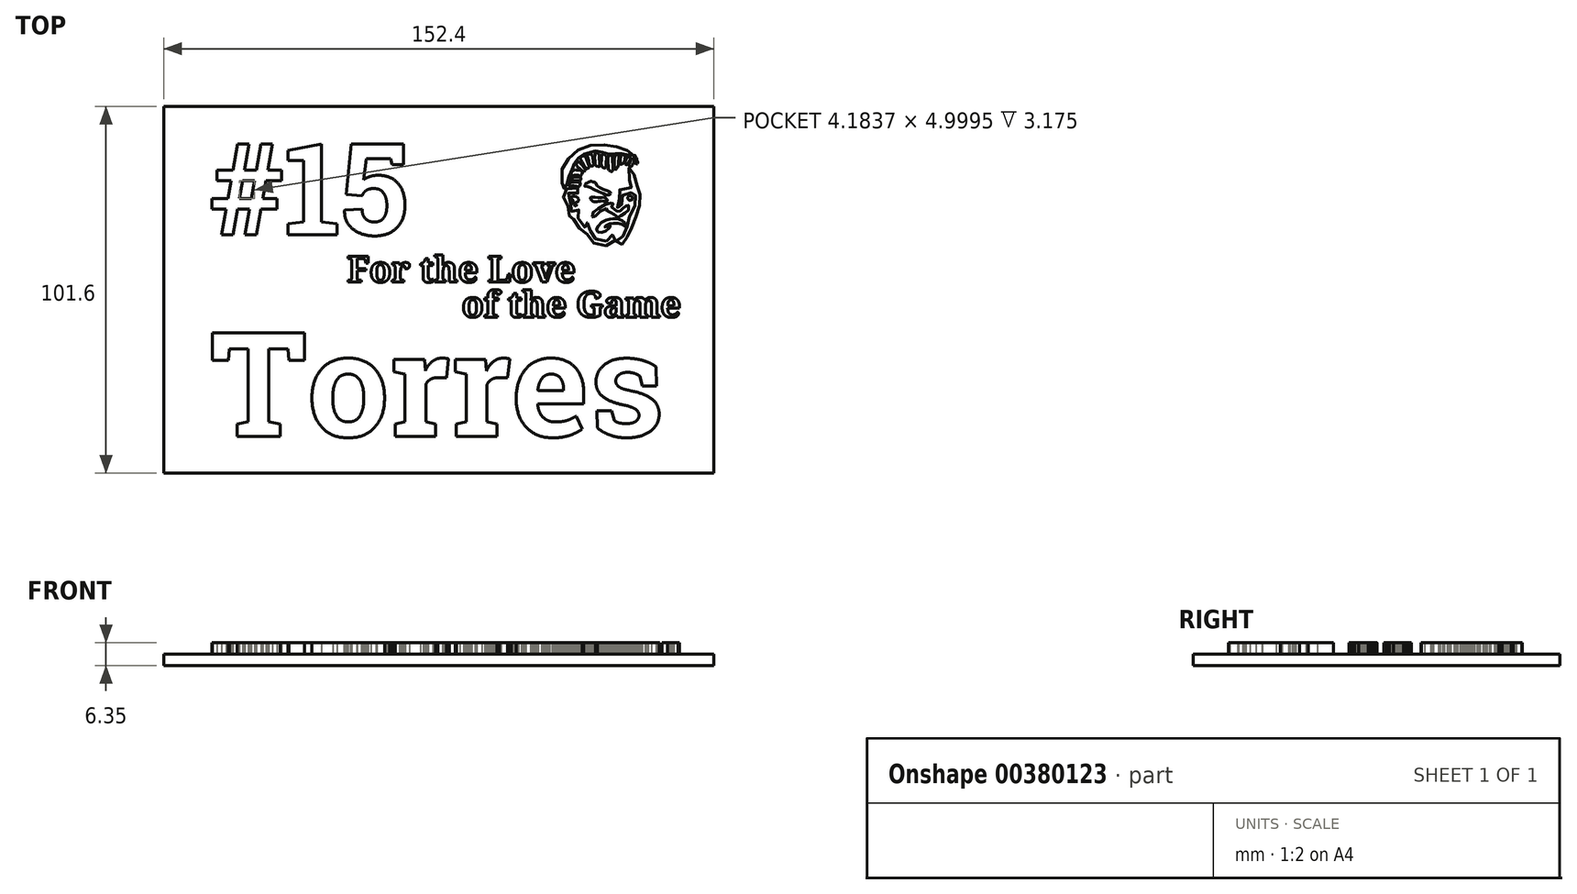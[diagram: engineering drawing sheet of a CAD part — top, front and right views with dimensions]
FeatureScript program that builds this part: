
annotation { "Feature Type Name" : "Feature", "Feature Type Description" : "" }
export const myFeature = defineFeature(function(context is Context, id is Id, definition is map)
    precondition{}
    {
        {
            var Q0;
            Q0=qCreatedBy(makeId("Top.planeOp"),FACE);
            var sketch = newSketch(context, id + "F0", { "sketchPlane" : qUnion([Q0])});
            skLineSegment(sketch, "E0.bottom", {"start": v(-75.13, 26) * mm, "end": v(77.27, 26) * mm});
            skLineSegment(sketch, "E0.top", {"start": v(-75.13, -75.6) * mm, "end": v(77.27, -75.6) * mm});
            skLineSegment(sketch, "E0.left", {"start": v(-75.13, 26) * mm, "end": v(-75.13, -75.6) * mm});
            skLineSegment(sketch, "E0.right", {"start": v(77.27, 26) * mm, "end": v(77.27, -75.6) * mm});
            skSolve(sketch);
        }
        {
            var Q0;
            Q0=makeQuery(id+"F0.imprint","IMPRINT",FACE,{"disambiguationData":[TD([[makeQuery(id+"F0.imprint","IMPRINT",EDGE,{"derivedFrom":sQuery(id+"F0.wireOp",EDGE,"E0.bottom")}),-1.0]])]});
            var sketch = newSketch(context, id + "F1", { "sketchPlane" : qUnion([Q0])});
            skFitSpline(sketch, "E1", {"points": [v(47.57, -11.3) * mm, v(48.35, -11.04) * mm, v(48.7, -10.35) * mm, v(49.04, -9.7) * mm, v(49.57, -9.46) * mm, v(50.02, -9.78) * mm, v(50.06, -10.58) * mm, v(49.74, -11.5) * mm, v(49.1, -12.15) * mm, v(47.63, -12.55) * mm, v(46.12, -12.5) * mm, v(44.61, -12.12) * mm, v(43.38, -11.34) * mm, v(42.6, -10.32) * mm, v(42.24, -9.52) * mm, v(42.15, -9.31) * mm, v(41.34, -8.82) * mm, v(40.33, -8.02) * mm, v(39.44, -7.2) * mm, v(38.67, -6.1) * mm, v(38.42, -5) * mm, v(38.42, -4.22) * mm, v(38.35, -4.2) * mm, v(37.68, -4.39) * mm, v(37.16, -4.27) * mm, v(36.95, -3.72) * mm, v(36.86, -2.5) * mm, v(36.8, -1.48) * mm, v(36.67, -1.07) * mm, v(35.77, 0.2) * mm, v(35.58, 1.07) * mm, v(35.86, 2.13) * mm, v(36.18, 2.7) * mm, v(36.53, 3.12) * mm, v(37.23, 3.22) * mm, v(39.03, 3.4) * mm, v(39.82, 3.34) * mm, v(40.19, 3.09) * mm, v(40.23, 2.45) * mm, v(39.66, 1.98) * mm, v(38.93, 1.9) * mm, v(38.59, 2.03) * mm, v(37.24, 2.03) * mm, v(36.72, 1.65) * mm, v(36.72, 0.85) * mm, v(37.32, -0.2) * mm, v(37.77, -1.18) * mm, v(37.85, -2.09) * mm, v(37.9, -3.1) * mm, v(37.99, -3.1) * mm, v(38.63, -3.1) * mm, v(39.4, -2.76) * mm, v(39.72, -2.59) * mm, v(39.8, -2.7) * mm, v(39.73, -3.22) * mm, v(39.6, -4) * mm, v(39.6, -4.77) * mm, v(40.1, -5.82) * mm, v(41.16, -7.15) * mm, v(41.6, -7.53) * mm, v(41.9, -7.56) * mm, v(41.89, -7.44) * mm, v(41.82, -6.61) * mm, v(42, -6.23) * mm, v(42.5, -6.3) * mm, v(42.8, -6.61) * mm, v(43.05, -7.98) * mm, v(43.22, -8.82) * mm, v(43.51, -9.54) * mm, v(44.12, -10.4) * mm, v(45.11, -11.01) * mm, v(46.32, -11.33) * mm, v(47.57, -11.3) * mm]});
            skFitSpline(sketch, "E2", {"points": [v(47.8, -7.3) * mm, v(47.13, -7.42) * mm, v(47.01, -7.42) * mm, v(47.13, -7.18) * mm, v(48.11, -6.65) * mm, v(49.11, -6.46) * mm, v(50.54, -6.45) * mm, v(51.76, -6.67) * mm, v(52.61, -7.21) * mm, v(52.82, -7.33) * mm, v(52.97, -7.12) * mm, v(52.7, -6.5) * mm, v(52.11, -5.74) * mm, v(50.6, -5.18) * mm, v(49.08, -5.16) * mm, v(48.46, -5.24) * mm, v(47.16, -5.6) * mm, v(45.65, -6.61) * mm, v(44.86, -7.78) * mm, v(44.9, -8.5) * mm, v(45.47, -8.94) * mm, v(46.7, -8.8) * mm, v(47.75, -8.16) * mm, v(48.56, -7.4) * mm, v(48.6, -7.12) * mm, v(47.8, -7.3) * mm]});
            skFitSpline(sketch, "E3", {"points": [v(51.85, -12.22) * mm, v(51.05, -12.44) * mm, v(50.33, -12.28) * mm, v(50.13, -11.73) * mm, v(50.52, -11.04) * mm, v(51.15, -10.86) * mm, v(51.76, -10.57) * mm, v(52.13, -10) * mm, v(52.3, -9.2) * mm, v(52.67, -8.25) * mm, v(53.2, -7.5) * mm, v(53.55, -6.76) * mm, v(53.63, -5.82) * mm, v(53.78, -4.85) * mm, v(54.49, -3.73) * mm, v(55.3, -2.73) * mm, v(55.42, -1.6) * mm, v(55.17, -0.4) * mm, v(55.2, 0.11) * mm, v(55.52, 1.32) * mm, v(55.57, 2.16) * mm, v(55.47, 2.42) * mm, v(54.99, 2.38) * mm, v(54.56, 2.14) * mm, v(53.7, 2.1) * mm, v(52.55, 2.06) * mm, v(52.07, 1.77) * mm, v(51.98, 1.02) * mm, v(52.2, 0.28) * mm, v(52.08, -0.6) * mm, v(51.72, -1.24) * mm, v(51.47, -1.75) * mm, v(51.5, -2.22) * mm, v(51.32, -2.4) * mm, v(50.6, -2.13) * mm, v(50.38, -1.6) * mm, v(50.64, -0.97) * mm, v(51, -0.17) * mm, v(51.06, 0.44) * mm, v(50.78, 1.07) * mm, v(50.66, 1.97) * mm, v(51.18, 2.9) * mm, v(52.12, 3.24) * mm, v(53.3, 3.36) * mm, v(54.52, 3.48) * mm, v(54.66, 3.6) * mm, v(54.38, 3.97) * mm, v(54, 4.8) * mm, v(53.79, 6.28) * mm, v(53.9, 7.94) * mm, v(53.79, 8.9) * mm, v(53.79, 9.1) * mm, v(54.03, 9.04) * mm, v(54.76, 8.52) * mm, v(55.13, 7.38) * mm, v(55.34, 5.97) * mm, v(55.56, 4.72) * mm, v(56.14, 3.87) * mm, v(56.71, 3.56) * mm, v(57.08, 2.91) * mm, v(56.95, 1.93) * mm, v(56.51, 0.55) * mm, v(56.4, -0.31) * mm, v(56.62, -1.36) * mm, v(56.69, -2.19) * mm, v(56.32, -3.56) * mm, v(55.4, -4.86) * mm, v(54.62, -5.8) * mm, v(54.5, -7.08) * mm, v(54.37, -8.24) * mm, v(53.76, -9.26) * mm, v(53.43, -9.82) * mm, v(53.28, -10.59) * mm, v(53.14, -11.27) * mm, v(52.34, -11.95) * mm, v(51.85, -12.22) * mm]});
            skFitSpline(sketch, "E4", {"points": [v(51.65, -4.28) * mm, v(52.13, -3.81) * mm, v(53.02, -3.37) * mm, v(53.66, -2.72) * mm, v(53.77, -1.9) * mm, v(53.38, -1.13) * mm, v(53.21, -1.15) * mm, v(53, -1.68) * mm, v(52.43, -2.14) * mm, v(51.8, -2.46) * mm, v(51.42, -2.92) * mm, v(50.93, -3.27) * mm, v(50.6, -3.17) * mm, v(50.13, -2.68) * mm, v(49.7, -2.46) * mm, v(49.28, -2.45) * mm, v(49, -1.98) * mm, v(49.06, -1.41) * mm, v(49.39, -0.94) * mm, v(49.4, -0.71) * mm, v(48.82, -0.74) * mm, v(47.56, -0.99) * mm, v(45.6, -2.02) * mm, v(44.06, -3.24) * mm, v(43.57, -3.77) * mm, v(43.7, -4.86) * mm, v(43.9, -4.88) * mm, v(44.45, -4.27) * mm, v(46.1, -2.93) * mm, v(47.41, -2.3) * mm, v(47.63, -2.3) * mm, v(47.73, -2.85) * mm, v(48.15, -3.33) * mm, v(48.9, -3.44) * mm, v(49.24, -3.55) * mm, v(49.84, -4.18) * mm, v(50.54, -4.68) * mm, v(51.18, -4.66) * mm, v(51.65, -4.28) * mm]});
            skFitSpline(sketch, "E5", {"points": [v(54.73, 0.39) * mm, v(54.77, 0.82) * mm, v(54.18, 1.2) * mm, v(53.55, 1.02) * mm, v(53.47, 0.3) * mm, v(54.02, 0) * mm, v(54.73, 0.39) * mm]});
            skFitSpline(sketch, "E6", {"points": [v(44.44, -0.47) * mm, v(43.66, -0.25) * mm, v(43.08, 0.44) * mm, v(43.14, 0.75) * mm, v(43.78, 0.8) * mm, v(46.74, 0.78) * mm, v(47.17, 0.7) * mm, v(47.78, -0.13) * mm, v(47.64, -0.32) * mm, v(46.64, -0.26) * mm, v(45.29, -0.32) * mm, v(44.44, -0.47) * mm]});
            skFitSpline(sketch, "E7", {"points": [v(46.65, 1.86) * mm, v(47.46, 1.48) * mm, v(48.33, 1.53) * mm, v(48.69, 2.02) * mm, v(48.54, 2.32) * mm, v(47.26, 2.83) * mm, v(45.32, 3.72) * mm, v(44.79, 4.23) * mm, v(44.53, 4.83) * mm, v(44.13, 5) * mm, v(43.88, 5) * mm, v(43.34, 5.26) * mm, v(43.09, 5.3) * mm, v(42.9, 5.05) * mm, v(42.6, 5.07) * mm, v(42.3, 4.85) * mm, v(42.2, 4.73) * mm, v(41.9, 4.72) * mm, v(41.8, 4.5) * mm, v(41.38, 4.05) * mm, v(41.56, 3.84) * mm, v(42.59, 3.74) * mm, v(43.78, 3.19) * mm, v(46.65, 1.86) * mm]});
            skFitSpline(sketch, "E8", {"points": [v(39.09, -1.2) * mm, v(38.85, -1.02) * mm, v(39.04, -0.63) * mm, v(39.6, -0.4) * mm, v(39.72, 0.33) * mm, v(39.01, 1.06) * mm, v(38.23, 1.1) * mm, v(37.7, 0.65) * mm, v(37.83, 0.29) * mm, v(38.12, 0.15) * mm, v(38.31, -0.34) * mm, v(38.52, -1.23) * mm, v(38.92, -1.63) * mm, v(39.18, -1.51) * mm, v(39.26, -1.2) * mm, v(39.09, -1.2) * mm]});
            skFitSpline(sketch, "E9", {"points": [v(35.18, 4.73) * mm, v(35.4, 3.4) * mm, v(35.76, 3.05) * mm, v(35.87, 3.13) * mm, v(36.08, 3.42) * mm, v(36.43, 3.67) * mm, v(36.66, 4.42) * mm, v(36.6, 5.36) * mm, v(37.02, 6.1) * mm, v(37.15, 6.7) * mm, v(37.23, 7.46) * mm, v(37.88, 8.4) * mm, v(38.45, 9.02) * mm, v(38.56, 9.75) * mm, v(38.74, 10.4) * mm, v(39.17, 10.98) * mm, v(39.64, 11.29) * mm, v(39.78, 11.9) * mm, v(40.12, 12.28) * mm, v(40.85, 12.68) * mm, v(41.65, 12.77) * mm, v(42.03, 12.99) * mm, v(42.91, 13.25) * mm, v(43.49, 13.17) * mm, v(43.91, 13.25) * mm, v(44.22, 13.54) * mm, v(44.87, 13.6) * mm, v(45.62, 13.32) * mm, v(46.3, 13.31) * mm, v(46.91, 13.3) * mm, v(47.51, 12.81) * mm, v(48.11, 12.71) * mm, v(48.8, 12.83) * mm, v(49.39, 12.68) * mm, v(50.13, 12.89) * mm, v(50.83, 12.96) * mm, v(51.35, 12.83) * mm, v(51.87, 12.94) * mm, v(52.53, 12.95) * mm, v(53.18, 12.6) * mm, v(53.93, 12.6) * mm, v(54.48, 12.4) * mm, v(54.65, 12.18) * mm, v(55.03, 12.55) * mm, v(54.73, 12.89) * mm, v(53.9, 13.45) * mm, v(51.53, 14.51) * mm, v(50.44, 14.76) * mm, v(49.1, 15.08) * mm, v(45.83, 15.4) * mm, v(43.17, 15.22) * mm, v(40.97, 14.54) * mm, v(38.6, 13.18) * mm, v(36.98, 11.4) * mm, v(35.34, 9.1) * mm, v(35.2, 8.1) * mm, v(35.18, 4.73) * mm]});
            skFitSpline(sketch, "E10", {"points": [v(39.4, 5) * mm, v(39.96, 4.99) * mm, v(40.23, 4.82) * mm, v(40.1, 4) * mm, v(39.64, 3.78) * mm, v(38.94, 3.9) * mm, v(37.89, 3.94) * mm, v(37.45, 3.8) * mm, v(37.1, 4.04) * mm, v(37.54, 4.84) * mm, v(38.3, 5) * mm, v(39.4, 5) * mm]});
            skFitSpline(sketch, "E11", {"points": [v(37.48, 5.07) * mm, v(37.11, 4.96) * mm, v(36.94, 5.2) * mm, v(37.34, 5.9) * mm, v(37.75, 6.14) * mm, v(39.96, 6.47) * mm, v(40.35, 6.2) * mm, v(40.47, 5.65) * mm, v(40.11, 5.36) * mm, v(39.64, 5.4) * mm, v(38.37, 5.41) * mm, v(37.48, 5.07) * mm]});
            skFitSpline(sketch, "E12", {"points": [v(38.14, 6.82) * mm, v(39.68, 6.88) * mm, v(40, 6.74) * mm, v(40.54, 7) * mm, v(40.85, 7.85) * mm, v(40.67, 8.1) * mm, v(39.1, 8.4) * mm, v(38.41, 8.3) * mm, v(37.9, 7.73) * mm, v(37.48, 6.86) * mm, v(37.68, 6.74) * mm, v(38.14, 6.82) * mm]});
            skFitSpline(sketch, "E13", {"points": [v(39.26, 9.59) * mm, v(41, 8.1) * mm, v(41.32, 7.94) * mm, v(41.68, 8.33) * mm, v(41.53, 8.74) * mm, v(40.44, 10.1) * mm, v(39.87, 10.6) * mm, v(39.5, 10.56) * mm, v(39.13, 10.09) * mm, v(39.26, 9.59) * mm]});
            skFitSpline(sketch, "E14", {"points": [v(40.75, 10.65) * mm, v(40.33, 11.47) * mm, v(40.46, 11.98) * mm, v(41.21, 12.34) * mm, v(41.77, 12.07) * mm, v(42.13, 11.12) * mm, v(42.72, 9.33) * mm, v(42.65, 8.96) * mm, v(42.12, 8.81) * mm, v(41.62, 9.07) * mm, v(40.75, 10.65) * mm]});
            skFitSpline(sketch, "E15", {"points": [v(42.43, 11.4) * mm, v(42.21, 12.24) * mm, v(42.3, 12.64) * mm, v(43, 12.81) * mm, v(43.54, 12.53) * mm, v(43.83, 11.13) * mm, v(44, 9.88) * mm, v(43.65, 9.47) * mm, v(42.94, 9.8) * mm, v(42.43, 11.4) * mm]});
            skFitSpline(sketch, "E16", {"points": [v(44.29, 12.06) * mm, v(44.36, 12.96) * mm, v(44.5, 13.26) * mm, v(44.93, 13.17) * mm, v(45.54, 12.55) * mm, v(45.55, 11.97) * mm, v(45.6, 9.45) * mm, v(45.5, 9.32) * mm, v(44.61, 9.6) * mm, v(44.4, 10.08) * mm, v(44.29, 12.06) * mm]});
            skFitSpline(sketch, "E17", {"points": [v(46.05, 10.51) * mm, v(46.15, 9.53) * mm, v(46.62, 9.04) * mm, v(47.1, 8.88) * mm, v(47.3, 9.08) * mm, v(47.48, 10.9) * mm, v(47.53, 12.07) * mm, v(47.34, 12.46) * mm, v(46.68, 12.84) * mm, v(46.32, 12.79) * mm, v(46.17, 11.97) * mm, v(46.05, 10.51) * mm]});
            skFitSpline(sketch, "E18", {"points": [v(48.03, 8.99) * mm, v(48.11, 8.48) * mm, v(48.48, 8.11) * mm, v(48.94, 7.92) * mm, v(49.21, 8.2) * mm, v(49.24, 10.23) * mm, v(49.16, 12.1) * mm, v(48.83, 12.47) * mm, v(48.44, 12.47) * mm, v(47.98, 12) * mm, v(47.93, 10.87) * mm, v(48.03, 8.99) * mm]});
            skFitSpline(sketch, "E19", {"points": [v(49.71, 9.45) * mm, v(49.86, 8.66) * mm, v(50.13, 8.48) * mm, v(50.3, 8.75) * mm, v(50.76, 9.43) * mm, v(50.85, 10.13) * mm, v(50.93, 12.16) * mm, v(50.81, 12.6) * mm, v(50.31, 12.66) * mm, v(49.83, 12.22) * mm, v(49.7, 11.19) * mm, v(49.71, 9.45) * mm]});
            skFitSpline(sketch, "E20", {"points": [v(51.32, 10.54) * mm, v(51.4, 11.84) * mm, v(51.7, 12.52) * mm, v(52.3, 12.55) * mm, v(52.72, 12.21) * mm, v(52.63, 11.54) * mm, v(52.29, 10.26) * mm, v(51.93, 10.06) * mm, v(51.44, 9.99) * mm, v(51.32, 10.54) * mm]});
            skFitSpline(sketch, "E21", {"points": [v(52.63, 10.38) * mm, v(52.83, 11.01) * mm, v(53.35, 11.9) * mm, v(53.66, 12.08) * mm, v(54.13, 11.71) * mm, v(53.9, 10.95) * mm, v(53.35, 10.1) * mm, v(53.17, 9.86) * mm, v(52.8, 9.99) * mm, v(52.63, 10.38) * mm]});
            skFitSpline(sketch, "E22", {"points": [v(53.86, 10.18) * mm, v(53.7, 9.9) * mm, v(53.81, 9.57) * mm, v(54.15, 9.28) * mm, v(54.42, 9.39) * mm, v(55.14, 10.6) * mm, v(55.26, 11.14) * mm, v(55.02, 11.54) * mm, v(54.8, 11.61) * mm, v(54.48, 11.27) * mm, v(53.86, 10.18) * mm]});
            skFitSpline(sketch, "E23", {"points": [v(55.24, 11.7) * mm, v(55.54, 11.38) * mm, v(55.58, 10.83) * mm, v(55.47, 10.49) * mm, v(55.7, 10.04) * mm, v(55.92, 10.02) * mm, v(56.2, 10.63) * mm, v(56.05, 10.85) * mm, v(55.85, 11.61) * mm, v(55.63, 12) * mm, v(55.42, 12.46) * mm, v(55.15, 12.4) * mm, v(55.09, 11.93) * mm, v(55.24, 11.7) * mm]});
            skText(sketch, "E24", { "text": "For the Love", "fontName": "NotoSerif-Bold.ttf"});
            skText(sketch, "E25", { "text": "of the Game", "fontName": "NotoSerif-Bold.ttf"});
            skText(sketch, "E26", { "text": "#15", "fontName": "RobotoSlab-Bold.ttf"});
            skText(sketch, "E27", { "text": "Torres", "fontName": "RobotoSlab-Bold.ttf"});
            const initialGuessF1  = {"E24": [-0.02433, -0.0227, 1, 0, 0.00716], "E25": [0.00742, -0.0324, 1, 0, 0.00716], "E26": [-0.06243, -0.00956, 1, 0, 0.0254], "E27": [-0.06243, -0.06544, 1, 0, 0.02903]};
            skSetInitialGuess(sketch, initialGuessF1);
            skSolve(sketch);
        }
        {
            var Q0;
            Q0=qSketchRegion(id+"F0",true);
            extrude(context, id + "F2", {"entities" : qUnion([Q0]), "depth" : 3.17 * mm});
        }
        {
            var Q0;
            Q0=qSketchRegion(id+"F1",true);
            extrude(context, id + "F3", {"entities" : qUnion([Q0]), "operationType" : NewBodyOperationType.ADD, "depth" : 6.35 * mm});
        }
    });
